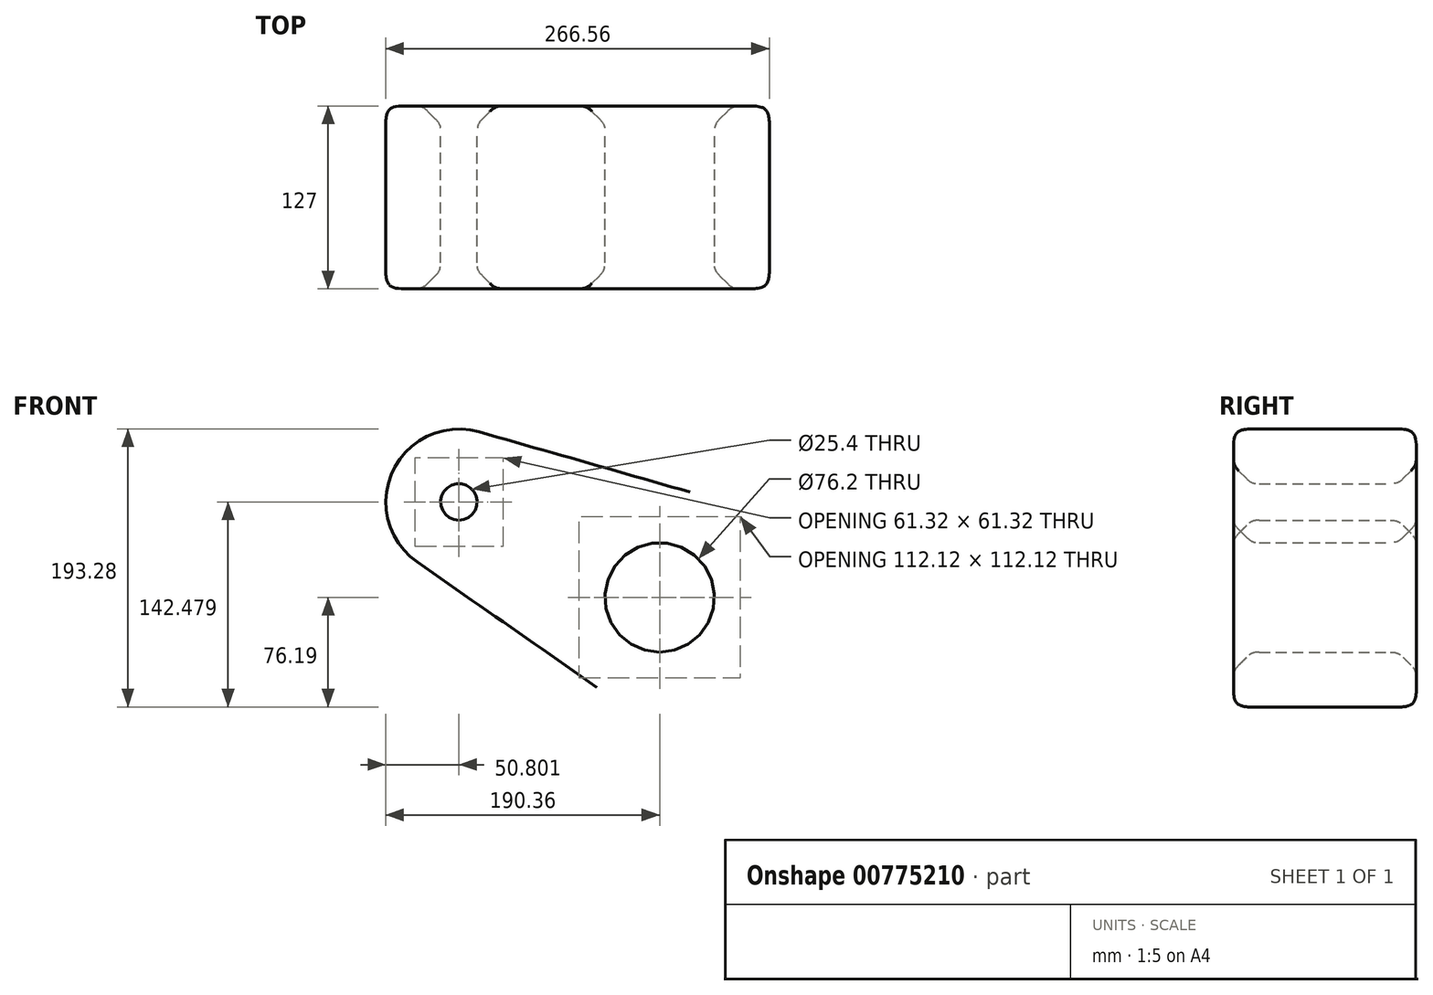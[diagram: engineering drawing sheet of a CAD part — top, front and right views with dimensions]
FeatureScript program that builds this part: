
annotation { "Feature Type Name" : "Feature", "Feature Type Description" : "" }
export const myFeature = defineFeature(function(context is Context, id is Id, definition is map)
    precondition{}
    {
        {
            var Q0;
            Q0=qCreatedBy(makeId("Front.planeOp"),FACE);
            var sketch = newSketch(context, id + "F0", { "sketchPlane" : qUnion([Q0])});
            skCircle(sketch, "E0", {"center": v(0, 0) * mm, "radius": 76.2 * mm});
            skCircle(sketch, "E1", {"center": v(0, 0) * mm, "radius": 38.1 * mm});
            skCircle(sketch, "E2", {"center": v(-139.56, 66.29) * mm, "radius": 50.8 * mm});
            skLineSegment(sketch, "E3", {"start": v(-125.6, 115.13) * mm, "end": v(20.93, 73.27) * mm});
            skLineSegment(sketch, "E4", {"start": v(-168.6, 24.61) * mm, "end": v(-43.56, -62.52) * mm});
            skCircle(sketch, "E5", {"center": v(-139.56, 66.29) * mm, "radius": 12.7 * mm});
            skSolve(sketch);
        }
        {
            var Q0;
            Q0=makeQuery(id+"F0.imprint","IMPRINT",FACE,{"disambiguationData":[TD([[makeQuery(id+"F0.imprint","IMPRINT",EDGE,{"derivedFrom":sQuery(id+"F0.wireOp",EDGE,"E5")}),-1.0]])]});
            var Q1;
            {var subQ0=sQuery(id+"F0.wireOp",EDGE,"E3");Q1=makeQuery(id+"F0.imprint","IMPRINT",FACE,{"disambiguationData":[TD([[makeQuery(id+"F0.imprint","IMPRINT",EDGE,{"derivedFrom":subQ0}),-1.0]])]});}
            var Q2;
            Q2=makeQuery(id+"F0.imprint","IMPRINT",FACE,{"disambiguationData":[TD([[makeQuery(id+"F0.imprint","IMPRINT",EDGE,{"derivedFrom":sQuery(id+"F0.wireOp",EDGE,"E1")}),-1.0]])]});
            extrude(context, id + "F1", {"entities" : qUnion([Q0, Q1, Q2]), "endBound" : BoundingType.SYMMETRIC, "depth" : 127 * mm, "offsetDistance" : 25.4 * mm});
        }
        {
            var Q0;
            Q0=makeQuery(id+"F1.opExtrude","CAP_EDGE",EDGE,{"disambiguationData":[OSD([sQuery(id+"F0.wireOp",EDGE,"E5")])],"isStart":false});
            var Q1;
            Q1=makeQuery(id+"F1.opExtrude","CAP_EDGE",EDGE,{"disambiguationData":[OSD([sQuery(id+"F0.wireOp",EDGE,"E1")])],"isStart":false});
            var Q2;
            Q2=makeQuery(id+"F1.opExtrude","CAP_EDGE",EDGE,{"disambiguationData":[OSD([sQuery(id+"F0.wireOp",EDGE,"E1")])],"isStart":true});
            var Q3;
            Q3=makeQuery(id+"F1.opExtrude","CAP_EDGE",EDGE,{"disambiguationData":[OSD([sQuery(id+"F0.wireOp",EDGE,"E5")])],"isStart":true});
            chamfer(context, id + "F2", {"entities" : qUnion([Q0, Q1, Q2, Q3]), "width" : 12.7 * mm, "tangentPropagation" : true});
        }
        {
            var Q0;
            Q0=makeQuery(id+"F1.opExtrude","CAP_EDGE",EDGE,{"disambiguationData":[OSD([sQuery(id+"F0.wireOp",EDGE,"E3")])],"isStart":false});
            var Q1;
            Q1=makeQuery(id+"F1.opExtrude","CAP_EDGE",EDGE,{"disambiguationData":[OSD([sQuery(id+"F0.wireOp",EDGE,"E3")])],"isStart":true});
            fillet(context, id + "F3", {"entities" : qUnion([Q0, Q1]), "radius" : 12.7 * mm, "tangentPropagation" : true, "rho" : .6, "crossSection" : FilletCrossSection.CONIC, "allowEdgeOverflow" : false});
        }
        {
            var Q0;
            {var subQ0=sQuery(id+"F0.wireOp",EDGE,"E5");Q0=makeQuery(id+"F2.opChamfer","BLEND_EDGE",EDGE,{"blendedFrom":[makeQuery(id+"F1.opExtrude","CAP_EDGE",EDGE,{"disambiguationData":[OSD([subQ0])],"isStart":true}),makeQuery(id+"F1.opExtrude","CAP_FACE",FACE,{"disambiguationData":[OSD([sQuery(id+"F0.wireOp",EDGE,"E0"),sQuery(id+"F0.wireOp",EDGE,"E1"),sQuery(id+"F0.wireOp",EDGE,"E2"),sQuery(id+"F0.wireOp",EDGE,"E3"),sQuery(id+"F0.wireOp",EDGE,"E4"),subQ0])],"isStart":true})],"blendedInto":[makeQuery(id+"F1.opExtrude","CAP_FACE",FACE,{"disambiguationData":[OSD([sQuery(id+"F0.wireOp",EDGE,"E0"),sQuery(id+"F0.wireOp",EDGE,"E1"),sQuery(id+"F0.wireOp",EDGE,"E2"),sQuery(id+"F0.wireOp",EDGE,"E3"),sQuery(id+"F0.wireOp",EDGE,"E4"),subQ0])],"isStart":true})]});}
            var Q1;
            {var subQ0=sQuery(id+"F0.wireOp",EDGE,"E1");Q1=makeQuery(id+"F2.opChamfer","BLEND_EDGE",EDGE,{"blendedFrom":[makeQuery(id+"F1.opExtrude","CAP_EDGE",EDGE,{"disambiguationData":[OSD([subQ0])],"isStart":true}),makeQuery(id+"F1.opExtrude","CAP_FACE",FACE,{"disambiguationData":[OSD([sQuery(id+"F0.wireOp",EDGE,"E0"),subQ0,sQuery(id+"F0.wireOp",EDGE,"E2"),sQuery(id+"F0.wireOp",EDGE,"E3"),sQuery(id+"F0.wireOp",EDGE,"E4"),sQuery(id+"F0.wireOp",EDGE,"E5")])],"isStart":true})],"blendedInto":[makeQuery(id+"F1.opExtrude","CAP_FACE",FACE,{"disambiguationData":[OSD([sQuery(id+"F0.wireOp",EDGE,"E0"),subQ0,sQuery(id+"F0.wireOp",EDGE,"E2"),sQuery(id+"F0.wireOp",EDGE,"E3"),sQuery(id+"F0.wireOp",EDGE,"E4"),sQuery(id+"F0.wireOp",EDGE,"E5")])],"isStart":true})]});}
            var Q2;
            {var subQ0=sQuery(id+"F0.wireOp",EDGE,"E5");Q2=makeQuery(id+"F2.opChamfer","BLEND_EDGE",EDGE,{"blendedFrom":[makeQuery(id+"F1.opExtrude","CAP_EDGE",EDGE,{"disambiguationData":[OSD([subQ0])],"isStart":true}),makeQuery(id+"F1.opExtrude","SWEPT_FACE",FACE,{"disambiguationData":[OSD([subQ0])]})],"blendedInto":[makeQuery(id+"F1.opExtrude","SWEPT_FACE",FACE,{"disambiguationData":[OSD([subQ0])]})]});}
            var Q3;
            {var subQ0=sQuery(id+"F0.wireOp",EDGE,"E1");Q3=makeQuery(id+"F2.opChamfer","BLEND_EDGE",EDGE,{"blendedFrom":[makeQuery(id+"F1.opExtrude","CAP_EDGE",EDGE,{"disambiguationData":[OSD([subQ0])],"isStart":true}),makeQuery(id+"F1.opExtrude","SWEPT_FACE",FACE,{"disambiguationData":[OSD([subQ0])]})],"blendedInto":[makeQuery(id+"F1.opExtrude","SWEPT_FACE",FACE,{"disambiguationData":[OSD([subQ0])]})]});}
            var Q4;
            {var subQ0=sQuery(id+"F0.wireOp",EDGE,"E1");Q4=makeQuery(id+"F2.opChamfer","BLEND_EDGE",EDGE,{"blendedFrom":[makeQuery(id+"F1.opExtrude","CAP_EDGE",EDGE,{"disambiguationData":[OSD([subQ0])],"isStart":false}),makeQuery(id+"F1.opExtrude","SWEPT_FACE",FACE,{"disambiguationData":[OSD([subQ0])]})],"blendedInto":[makeQuery(id+"F1.opExtrude","SWEPT_FACE",FACE,{"disambiguationData":[OSD([subQ0])]})]});}
            var Q5;
            {var subQ0=sQuery(id+"F0.wireOp",EDGE,"E1");Q5=makeQuery(id+"F2.opChamfer","BLEND_EDGE",EDGE,{"blendedFrom":[makeQuery(id+"F1.opExtrude","CAP_EDGE",EDGE,{"disambiguationData":[OSD([subQ0])],"isStart":false}),makeQuery(id+"F1.opExtrude","CAP_FACE",FACE,{"disambiguationData":[OSD([sQuery(id+"F0.wireOp",EDGE,"E0"),subQ0,sQuery(id+"F0.wireOp",EDGE,"E2"),sQuery(id+"F0.wireOp",EDGE,"E3"),sQuery(id+"F0.wireOp",EDGE,"E4"),sQuery(id+"F0.wireOp",EDGE,"E5")])],"isStart":false})],"blendedInto":[makeQuery(id+"F1.opExtrude","CAP_FACE",FACE,{"disambiguationData":[OSD([sQuery(id+"F0.wireOp",EDGE,"E0"),subQ0,sQuery(id+"F0.wireOp",EDGE,"E2"),sQuery(id+"F0.wireOp",EDGE,"E3"),sQuery(id+"F0.wireOp",EDGE,"E4"),sQuery(id+"F0.wireOp",EDGE,"E5")])],"isStart":false})]});}
            var Q6;
            {var subQ0=sQuery(id+"F0.wireOp",EDGE,"E5");Q6=makeQuery(id+"F2.opChamfer","BLEND_EDGE",EDGE,{"blendedFrom":[makeQuery(id+"F1.opExtrude","CAP_EDGE",EDGE,{"disambiguationData":[OSD([subQ0])],"isStart":false}),makeQuery(id+"F1.opExtrude","CAP_FACE",FACE,{"disambiguationData":[OSD([sQuery(id+"F0.wireOp",EDGE,"E0"),sQuery(id+"F0.wireOp",EDGE,"E1"),sQuery(id+"F0.wireOp",EDGE,"E2"),sQuery(id+"F0.wireOp",EDGE,"E3"),sQuery(id+"F0.wireOp",EDGE,"E4"),subQ0])],"isStart":false})],"blendedInto":[makeQuery(id+"F1.opExtrude","CAP_FACE",FACE,{"disambiguationData":[OSD([sQuery(id+"F0.wireOp",EDGE,"E0"),sQuery(id+"F0.wireOp",EDGE,"E1"),sQuery(id+"F0.wireOp",EDGE,"E2"),sQuery(id+"F0.wireOp",EDGE,"E3"),sQuery(id+"F0.wireOp",EDGE,"E4"),subQ0])],"isStart":false})]});}
            var Q7;
            {var subQ0=sQuery(id+"F0.wireOp",EDGE,"E5");Q7=makeQuery(id+"F2.opChamfer","BLEND_EDGE",EDGE,{"blendedFrom":[makeQuery(id+"F1.opExtrude","CAP_EDGE",EDGE,{"disambiguationData":[OSD([subQ0])],"isStart":false}),makeQuery(id+"F1.opExtrude","SWEPT_FACE",FACE,{"disambiguationData":[OSD([subQ0])]})],"blendedInto":[makeQuery(id+"F1.opExtrude","SWEPT_FACE",FACE,{"disambiguationData":[OSD([subQ0])]})]});}
            fillet(context, id + "F4", {"entities" : qUnion([Q0, Q1, Q2, Q3, Q4, Q5, Q6, Q7]), "radius" : 12.7 * mm, "tangentPropagation" : true, "rho" : .6, "crossSection" : FilletCrossSection.CONIC, "allowEdgeOverflow" : false});
        }
    });
